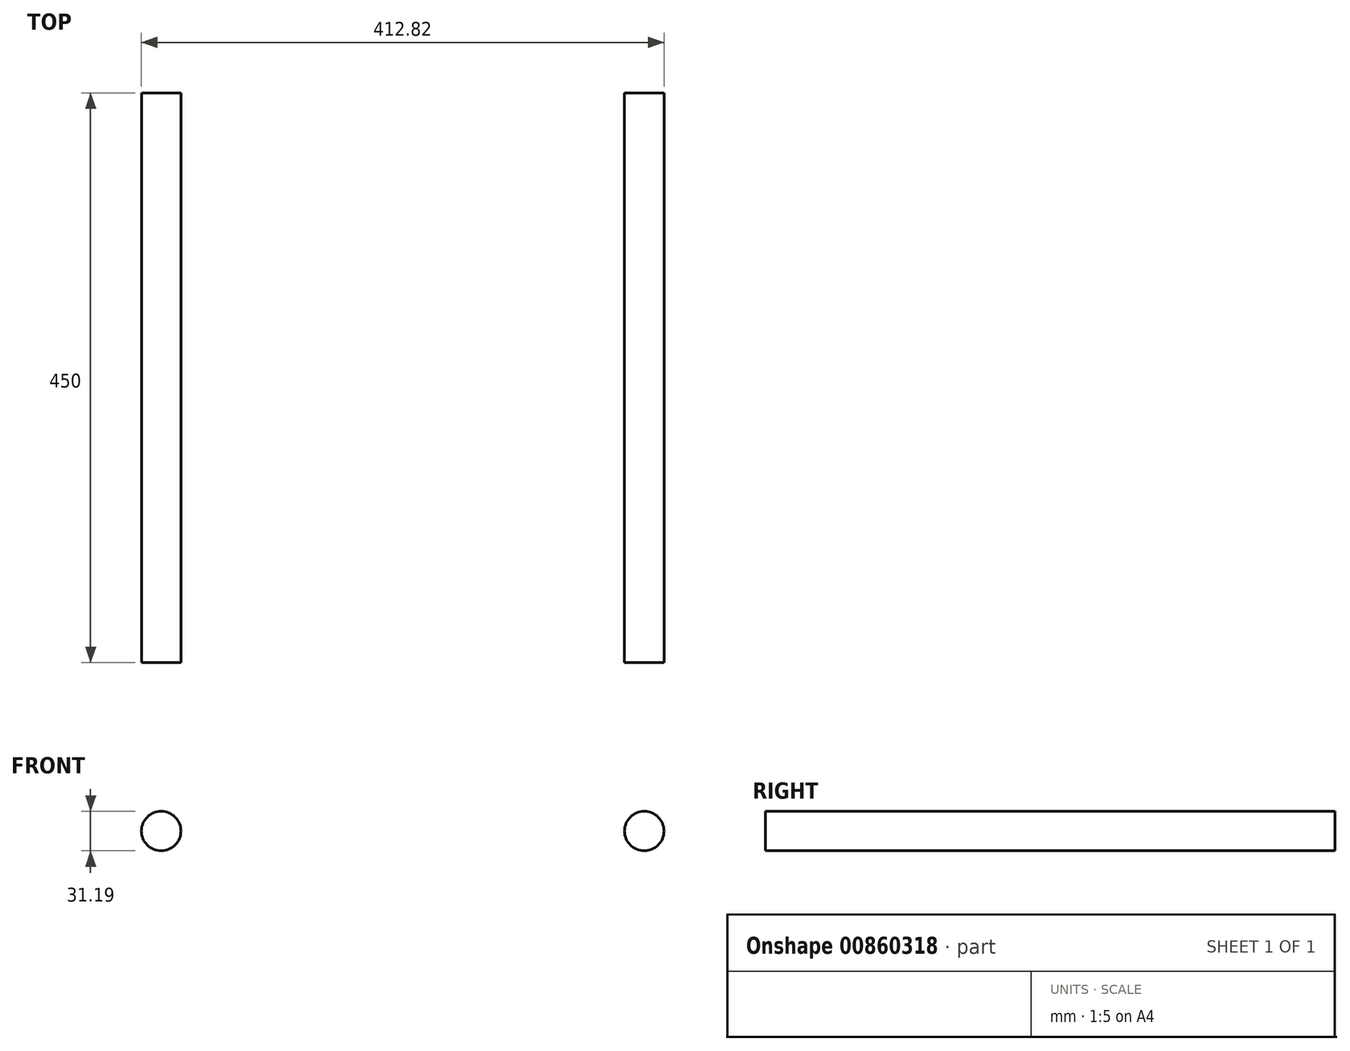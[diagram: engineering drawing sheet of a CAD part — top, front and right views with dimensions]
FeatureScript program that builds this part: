
annotation { "Feature Type Name" : "Feature", "Feature Type Description" : "" }
export const myFeature = defineFeature(function(context is Context, id is Id, definition is map)
    precondition{}
    {
        {
            var Q0;
            Q0=qCreatedBy(makeId("Front.planeOp"),FACE);
            var sketch = newSketch(context, id + "F0", { "sketchPlane" : qUnion([Q0])});
            skCircle(sketch, "E0", {"center": v(190.81, -58.64) * mm, "radius": 15.6 * mm});
            skCircle(sketch, "E1", {"center": v(190.81, -58.64) * mm, "radius": 31.87 * mm});
            skSolve(sketch);
        }
        {
            var Q0;
            Q0=makeQuery(id+"F0.imprint","IMPRINT",FACE,{"disambiguationData":[TD([[makeQuery(id+"F0.imprint","IMPRINT",EDGE,{"derivedFrom":sQuery(id+"F0.wireOp",EDGE,"E0")}),1.0]])]});
            extrude(context, id + "F1", {"entities" : qUnion([Q0]), "endBound" : BoundingType.SYMMETRIC, "depth" : 450 * mm, "offsetDistance" : 25 * mm});
        }
        {
            var Q0;
            Q0=makeQuery(id+"F1.opExtrude","SWEPT_BODY",BODY,{"disambiguationData":[OSD([sQuery(id+"F0.wireOp",EDGE,"E0")])]});
            var Q1;
            Q1=qCreatedBy(makeId("Right.planeOp"),FACE);
            mirror(context, id + "F2", {"entities" : qUnion([Q0]), "mirrorPlane" : qUnion([Q1])});
        }
    });
